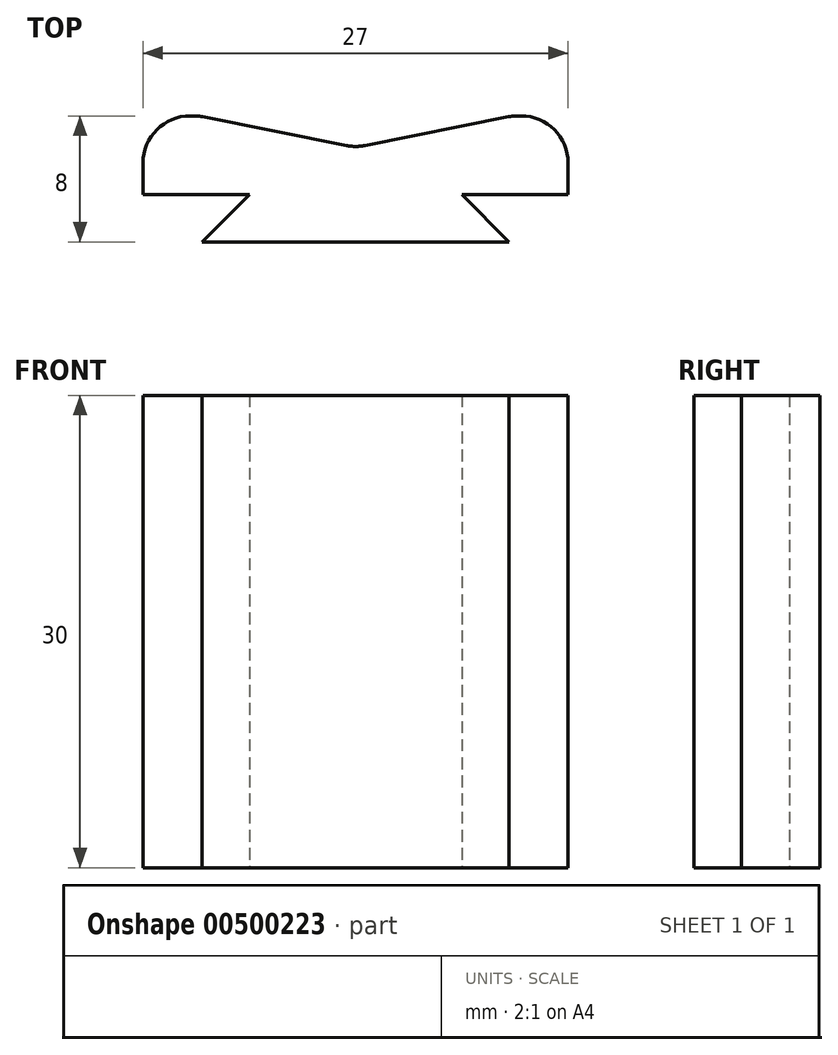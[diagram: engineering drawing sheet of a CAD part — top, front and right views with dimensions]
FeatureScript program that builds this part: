
annotation { "Feature Type Name" : "Feature", "Feature Type Description" : "" }
export const myFeature = defineFeature(function(context is Context, id is Id, definition is map)
    precondition{}
    {
        {
            var Q0;
            Q0=qCreatedBy(makeId("Top.planeOp"),FACE);
            var sketch = newSketch(context, id + "F0", { "sketchPlane" : qUnion([Q0])});
            skLineSegment(sketch, "E0", {"start": v(0, 0) * mm, "end": v(-13.5, 0) * mm});
            skLineSegment(sketch, "E1", {"start": v(-13.5, 0) * mm, "end": v(-13.5, 5) * mm});
            skLineSegment(sketch, "E2", {"start": v(-13.5, 5) * mm, "end": v(-10, 5) * mm});
            skLineSegment(sketch, "E3", {"start": v(-10, 5) * mm, "end": v(0, 3) * mm});
            skLineSegment(sketch, "E4", {"start": v(0, 3) * mm, "end": v(0, 0) * mm});
            skLineSegment(sketch, "E5.MirrorCS", {"start": v(10, 5) * mm, "end": v(0, 3) * mm});
            skLineSegment(sketch, "E6.MirrorCS", {"start": v(13.5, 5) * mm, "end": v(10, 5) * mm});
            skLineSegment(sketch, "E7.MirrorCS", {"start": v(13.5, 0) * mm, "end": v(13.5, 5) * mm});
            skLineSegment(sketch, "E8.MirrorCS", {"start": v(0, 0) * mm, "end": v(13.5, 0) * mm});
            skLineSegment(sketch, "E9", {"start": v(-6.75, 0) * mm, "end": v(-9.75, -3) * mm});
            skLineSegment(sketch, "E10", {"start": v(-9.75, -3) * mm, "end": v(0, -3) * mm});
            skLineSegment(sketch, "E11", {"start": v(0, -3) * mm, "end": v(0, 0) * mm});
            skLineSegment(sketch, "E12.MirrorCS", {"start": v(6.75, 0) * mm, "end": v(9.75, -3) * mm});
            skLineSegment(sketch, "E13.MirrorCS", {"start": v(9.75, -3) * mm, "end": v(0, -3) * mm});
            skSolve(sketch);
        }
        {
            var Q0;
            {var subQ0=sQuery(id+"F0.wireOp",EDGE,"E1");Q0=makeQuery(id+"F0.imprint","IMPRINT",FACE,{"disambiguationData":[TD([[makeQuery(id+"F0.imprint","IMPRINT",EDGE,{"derivedFrom":subQ0}),-1.0]])]});}
            var Q1;
            {var subQ2=sQuery(id+"F0.wireOp",EDGE,"E9");Q1=makeQuery(id+"F0.imprint","IMPRINT",FACE,{"disambiguationData":[TD([[makeQuery(id+"F0.imprint","IMPRINT",EDGE,{"derivedFrom":subQ2}),1.0]])]});}
            var Q2;
            {var subQ0=sQuery(id+"F0.wireOp",EDGE,"E11");Q2=makeQuery(id+"F0.imprint","IMPRINT",FACE,{"disambiguationData":[TD([[makeQuery(id+"F0.imprint","IMPRINT",EDGE,{"derivedFrom":subQ0}),-1.0]])]});}
            var Q3;
            {var subQ1=sQuery(id+"F0.wireOp",EDGE,"E4");Q3=makeQuery(id+"F0.imprint","IMPRINT",FACE,{"disambiguationData":[TD([[makeQuery(id+"F0.imprint","IMPRINT",EDGE,{"derivedFrom":subQ1}),1.0]])]});}
            extrude(context, id + "F1", {"entities" : qUnion([Q0, Q1, Q2, Q3]), "depth" : 30 * mm});
        }
        {
            var Q0;
            Q0=makeQuery(id+"F1.opExtrude","SWEPT_EDGE",EDGE,{"disambiguationData":[OSD([sQuery(id+"F0.wireOp",EDGE,"E1"),sQuery(id+"F0.wireOp",EDGE,"E2")])]});
            var Q1;
            Q1=makeQuery(id+"F1.opExtrude","SWEPT_EDGE",EDGE,{"disambiguationData":[OSD([sQuery(id+"F0.wireOp",EDGE,"E2"),sQuery(id+"F0.wireOp",EDGE,"E3")])]});
            var Q2;
            Q2=makeQuery(id+"F1.opExtrude","SWEPT_EDGE",EDGE,{"disambiguationData":[OSD([sQuery(id+"F0.wireOp",EDGE,"E6.MirrorCS"),sQuery(id+"F0.wireOp",EDGE,"E7.MirrorCS")])]});
            var Q3;
            Q3=makeQuery(id+"F1.opExtrude","SWEPT_EDGE",EDGE,{"disambiguationData":[OSD([sQuery(id+"F0.wireOp",EDGE,"E5.MirrorCS"),sQuery(id+"F0.wireOp",EDGE,"E6.MirrorCS")])]});
            var Q4;
            Q4=makeQuery(id+"F1.opExtrude","SWEPT_EDGE",EDGE,{"disambiguationData":[OSD([sQuery(id+"F0.wireOp",EDGE,"E3"),sQuery(id+"F0.wireOp",EDGE,"E4"),sQuery(id+"F0.wireOp",EDGE,"E5.MirrorCS")])]});
            fillet(context, id + "F2", {"entities" : qUnion([Q0, Q1, Q2, Q3, Q4]), "radius" : 3 * mm, "tangentPropagation" : true, "allowEdgeOverflow" : false});
        }
    });
